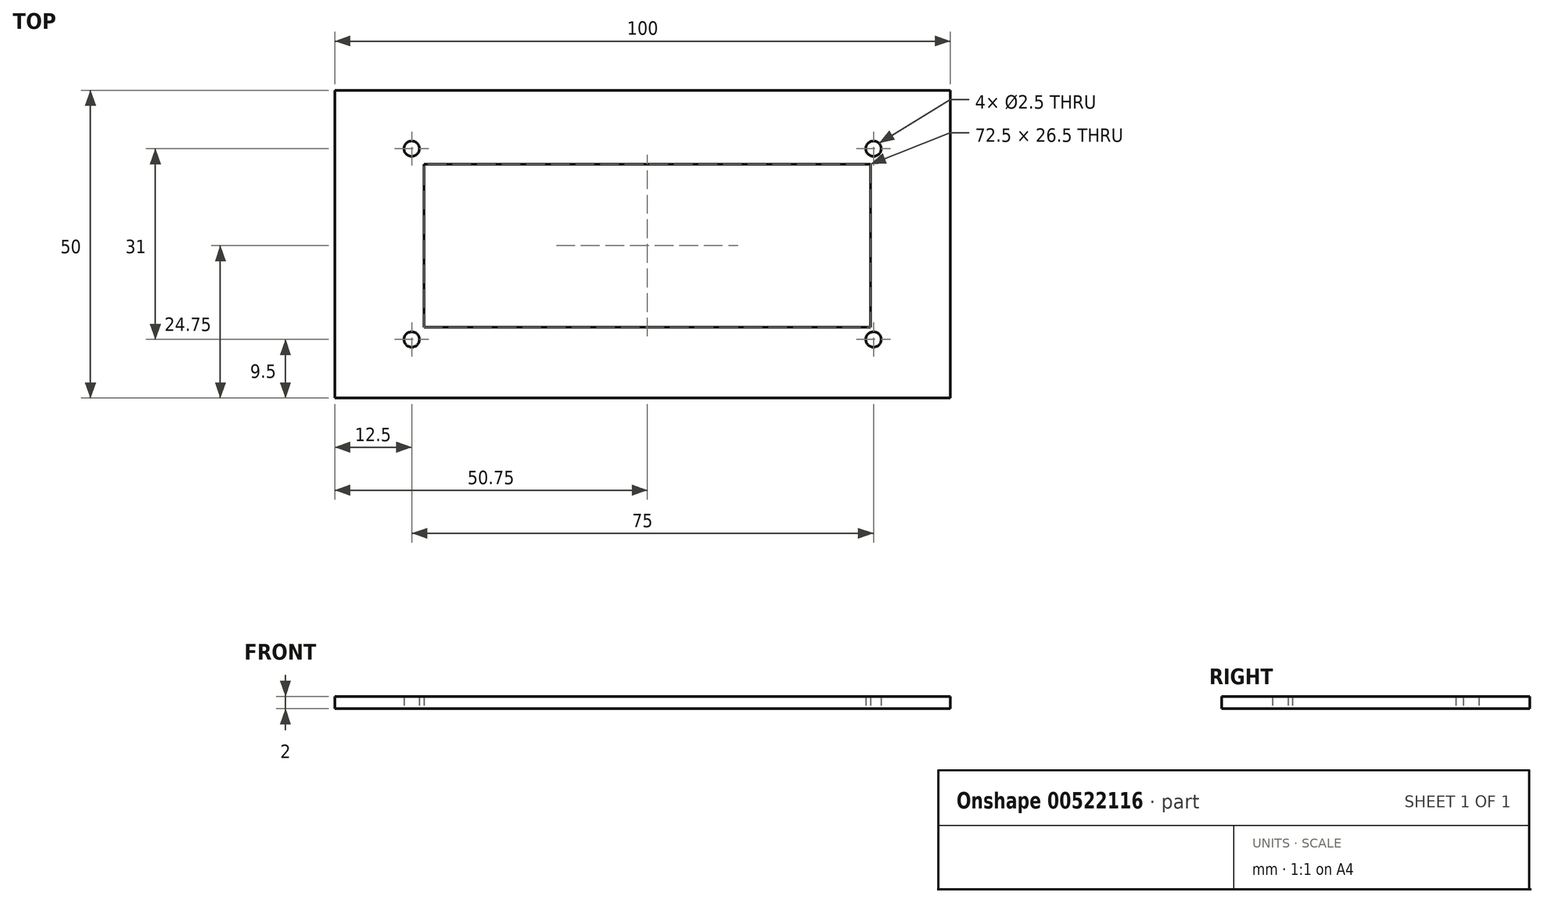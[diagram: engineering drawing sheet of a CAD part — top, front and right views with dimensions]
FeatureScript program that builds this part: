
annotation { "Feature Type Name" : "Feature", "Feature Type Description" : "" }
export const myFeature = defineFeature(function(context is Context, id is Id, definition is map)
    precondition{}
    {
        {
            var Q0;
            Q0=qCreatedBy(makeId("Top.planeOp"),FACE);
            var sketch = newSketch(context, id + "F0", { "sketchPlane" : qUnion([Q0])});
            skLineSegment(sketch, "E0.bottom", {"start": v(50, 25) * mm, "end": v(-50, 25) * mm});
            skLineSegment(sketch, "E0.top", {"start": v(50, -25) * mm, "end": v(-50, -25) * mm});
            skLineSegment(sketch, "E0.left", {"start": v(50, 25) * mm, "end": v(50, -25) * mm});
            skLineSegment(sketch, "E0.right", {"start": v(-50, 25) * mm, "end": v(-50, -25) * mm});
            skPoint(sketch, "E0.middle", {"position": v(0, 0) * mm});
            skLineSegment(sketch, "E1.bottom", {"start": v(37.5, 15.5) * mm, "end": v(-37.5, 15.5) * mm, "construction": true});
            skLineSegment(sketch, "E1.top", {"start": v(37.5, -15.5) * mm, "end": v(-37.5, -15.5) * mm, "construction": true});
            skLineSegment(sketch, "E1.left", {"start": v(37.5, 15.5) * mm, "end": v(37.5, -15.5) * mm, "construction": true});
            skLineSegment(sketch, "E1.right", {"start": v(-37.5, 15.5) * mm, "end": v(-37.5, -15.5) * mm, "construction": true});
            skPoint(sketch, "E2", {"position": v(-37.5, 15.5) * mm});
            skPoint(sketch, "E3", {"position": v(-37.5, -15.5) * mm});
            skPoint(sketch, "E4", {"position": v(37.5, -15.5) * mm});
            skPoint(sketch, "E5", {"position": v(37.5, 15.5) * mm});
            skLineSegment(sketch, "E6.bottom", {"start": v(-35.5, -13.5) * mm, "end": v(37, -13.5) * mm});
            skLineSegment(sketch, "E6.top", {"start": v(-35.5, 13) * mm, "end": v(37, 13) * mm});
            skLineSegment(sketch, "E6.left", {"start": v(-35.5, -13.5) * mm, "end": v(-35.5, 13) * mm});
            skLineSegment(sketch, "E6.right", {"start": v(37, -13.5) * mm, "end": v(37, 13) * mm});
            skSolve(sketch);
        }
        {
            var Q0;
            Q0=makeQuery(id+"F0.imprint","IMPRINT",FACE,{"disambiguationData":[TD([[makeQuery(id+"F0.imprint","IMPRINT",EDGE,{"derivedFrom":sQuery(id+"F0.wireOp",EDGE,"E0.bottom")}),1.0]])]});
            extrude(context, id + "F1", {"entities" : qUnion([Q0]), "depth" : 2 * mm, "offsetDistance" : 25 * mm});
        }
        {
            var Q0;
            Q0=sQuery(id+"F0.wireOp",VERTEX,"E3");
            var Q1;
            Q1=sQuery(id+"F0.wireOp",VERTEX,"E2");
            var Q2;
            Q2=sQuery(id+"F0.wireOp",VERTEX,"E5");
            var Q3;
            Q3=sQuery(id+"F0.wireOp",VERTEX,"E4");
            var Q4;
            Q4=makeQuery(id+"F1.opExtrude","SWEPT_BODY",BODY,{"disambiguationData":[OSD([sQuery(id+"F0.wireOp",EDGE,"E0.bottom"),sQuery(id+"F0.wireOp",EDGE,"E0.top"),sQuery(id+"F0.wireOp",EDGE,"E0.left"),sQuery(id+"F0.wireOp",EDGE,"E0.right"),sQuery(id+"F0.wireOp",EDGE,"fecaa5aa-416a-459a-90f7-f8e3abe4e8bc.bottom"),sQuery(id+"F0.wireOp",EDGE,"fecaa5aa-416a-459a-90f7-f8e3abe4e8bc.top"),sQuery(id+"F0.wireOp",EDGE,"fecaa5aa-416a-459a-90f7-f8e3abe4e8bc.left"),sQuery(id+"F0.wireOp",EDGE,"fecaa5aa-416a-459a-90f7-f8e3abe4e8bc.right")])]});
            hole(context, id + "F2", {"style" : HoleStyle.SIMPLE, "endStyle" : HoleEndStyle.THROUGH, "oppositeDirection" : true, "holeDiameter" : 2.5 * mm, "isTappedThrough" : true, "tappedDepth" : 12 * mm, "tapClearance" : 3, "locations" : qUnion([Q0, Q1, Q2, Q3]), "scope" : qUnion([Q4])});
        }
    });
